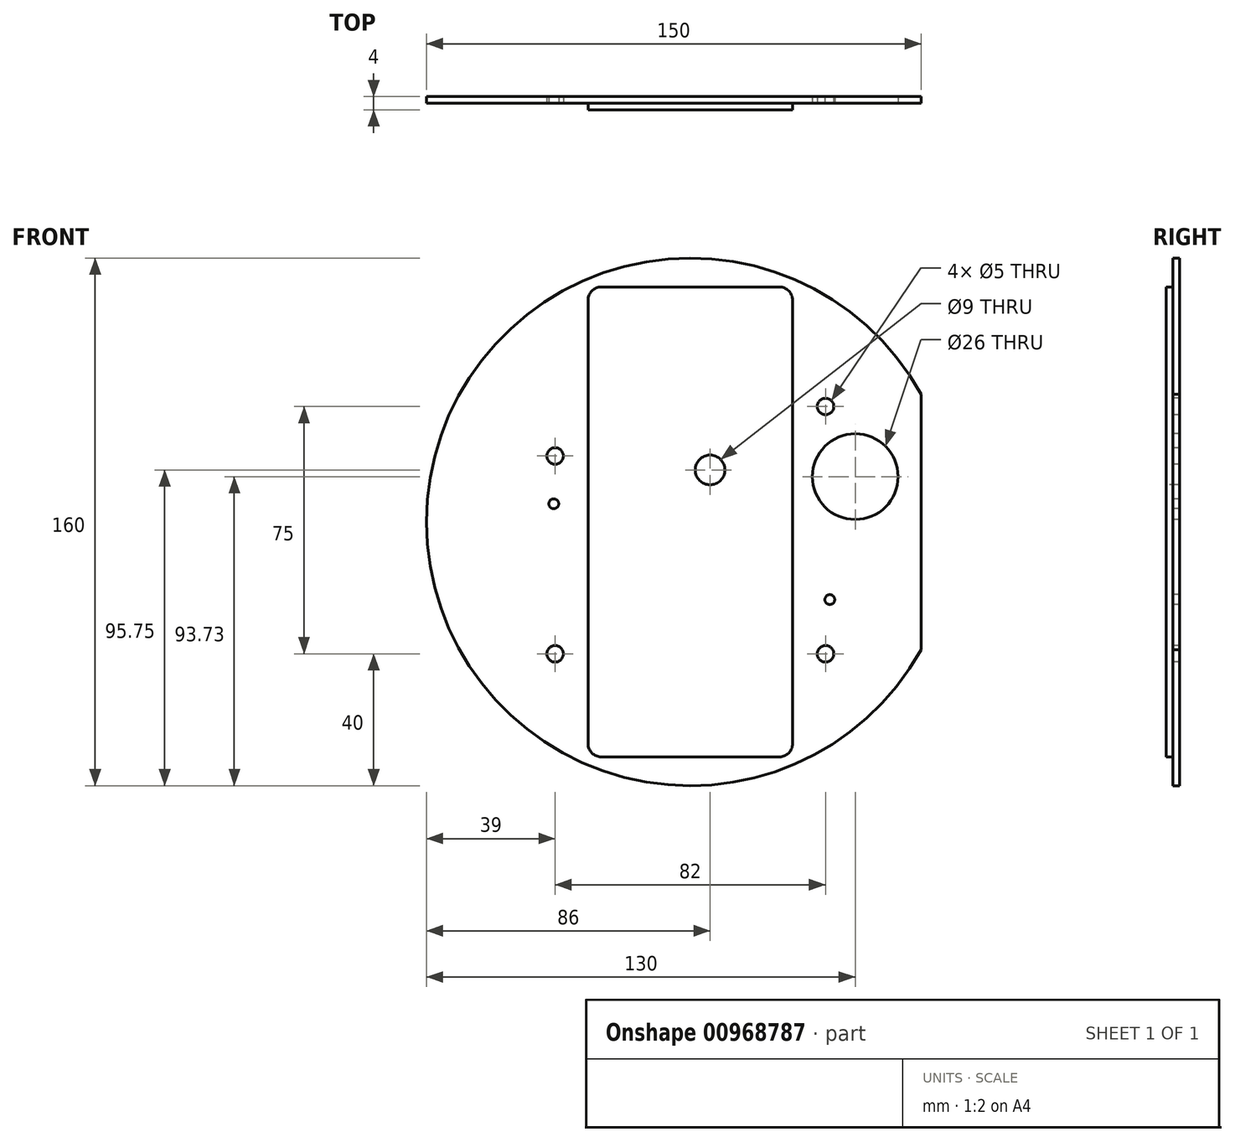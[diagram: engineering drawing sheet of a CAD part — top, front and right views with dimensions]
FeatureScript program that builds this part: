
annotation { "Feature Type Name" : "Feature", "Feature Type Description" : "" }
export const myFeature = defineFeature(function(context is Context, id is Id, definition is map)
    precondition{}
    {
        {
            var Q0;
            Q0=qCreatedBy(makeId("Front.planeOp"),FACE);
            var sketch = newSketch(context, id + "F0", { "sketchPlane" : qUnion([Q0])});
            skArc(sketch, "E0", {"start": v(70, -38.73) * mm, "mid": v(-80, 0) * mm, "end": v(70, 38.73) * mm});
            skLineSegment(sketch, "E1", {"start": v(70, 38.73) * mm, "end": v(70, -38.73) * mm});
            skSolve(sketch);
        }
        {
            var Q0;
            Q0 = qSketchRegion(id + "F0", true);
            extrude(context, id + "F1", {"entities" : qUnion([Q0]), "depth" : 2 * mm, "offsetDistance" : 25 * mm});
        }
        {
            var Q0;
            Q0=makeQuery(id+"F1.opExtrude","CAP_FACE",FACE,{"disambiguationData":[OSD([sQuery(id+"F0.wireOp",EDGE,"E0"),sQuery(id+"F0.wireOp",EDGE,"E1")])],"isStart":false});
            var sketch = newSketch(context, id + "F2", { "sketchPlane" : qUnion([Q0])});
            skLineSegment(sketch, "E2.bottom", {"start": v(-31, 71.25) * mm, "end": v(31, 71.25) * mm});
            skLineSegment(sketch, "E2.top", {"start": v(-31, -71.25) * mm, "end": v(31, -71.25) * mm});
            skLineSegment(sketch, "E2.left", {"start": v(-31, 71.25) * mm, "end": v(-31, -71.25) * mm});
            skLineSegment(sketch, "E2.right", {"start": v(31, 71.25) * mm, "end": v(31, -71.25) * mm});
            skSolve(sketch);
        }
        {
            var Q0;
            Q0 = qSketchRegion(id + "F2", true);
            extrude(context, id + "F3", {"entities" : qUnion([Q0]), "operationType" : NewBodyOperationType.ADD, "depth" : 2 * mm, "offsetDistance" : 25 * mm});
        }
        {
            var Q0;
            Q0=makeQuery(id+"F3.opExtrude","SWEPT_EDGE",EDGE,{"disambiguationData":[OSD([sQuery(id+"F2.wireOp",EDGE,"E2.top"),sQuery(id+"F2.wireOp",EDGE,"E2.left")])]});
            var Q1;
            Q1=makeQuery(id+"F3.opExtrude","SWEPT_EDGE",EDGE,{"disambiguationData":[OSD([sQuery(id+"F2.wireOp",EDGE,"E2.top"),sQuery(id+"F2.wireOp",EDGE,"E2.right")])]});
            var Q2;
            Q2=makeQuery(id+"F3.opExtrude","SWEPT_EDGE",EDGE,{"disambiguationData":[OSD([sQuery(id+"F2.wireOp",EDGE,"E2.bottom"),sQuery(id+"F2.wireOp",EDGE,"E2.right")])]});
            var Q3;
            Q3=makeQuery(id+"F3.opExtrude","SWEPT_EDGE",EDGE,{"disambiguationData":[OSD([sQuery(id+"F2.wireOp",EDGE,"E2.bottom"),sQuery(id+"F2.wireOp",EDGE,"E2.left")])]});
            fillet(context, id + "F4", {"entities" : qUnion([Q0, Q1, Q2, Q3]), "radius" : 4 * mm, "tangentPropagation" : true, "allowEdgeOverflow" : false});
        }
        {
            var Q0;
            Q0=makeQuery(id+"F3.opExtrude","CAP_FACE",FACE,{"disambiguationData":[OSD([sQuery(id+"F2.wireOp",EDGE,"E2.bottom"),sQuery(id+"F2.wireOp",EDGE,"E2.top"),sQuery(id+"F2.wireOp",EDGE,"E2.left"),sQuery(id+"F2.wireOp",EDGE,"E2.right")])],"isStart":false});
            var sketch = newSketch(context, id + "F5", { "sketchPlane" : qUnion([Q0])});
            skCircle(sketch, "E3", {"center": v(6, 15.75) * mm, "radius": 4.5 * mm});
            skSolve(sketch);
        }
        {
            var Q0;
            Q0 = qSketchRegion(id + "F5", true);
            extrude(context, id + "F6", {"entities" : qUnion([Q0]), "operationType" : NewBodyOperationType.REMOVE, "oppositeDirection" : true, "depth" : 4 * mm, "offsetDistance" : 25 * mm});
        }
        {
            var Q0;
            Q0=makeQuery(id+"F1.opExtrude","CAP_FACE",FACE,{"disambiguationData":[OSD([sQuery(id+"F0.wireOp",EDGE,"E0"),sQuery(id+"F0.wireOp",EDGE,"E1")])],"isStart":false});
            var sketch = newSketch(context, id + "F7", { "sketchPlane" : qUnion([Q0])});
            skCircle(sketch, "E4", {"center": v(50, 13.73) * mm, "radius": 13 * mm});
            skSolve(sketch);
        }
        {
            var Q0;
            Q0 = qSketchRegion(id + "F7", true);
            extrude(context, id + "F8", {"entities" : qUnion([Q0]), "operationType" : NewBodyOperationType.REMOVE, "oppositeDirection" : true, "depth" : 2 * mm, "offsetDistance" : 25 * mm});
        }
        {
            var Q0;
            Q0=makeQuery(id+"F1.opExtrude","CAP_FACE",FACE,{"disambiguationData":[OSD([sQuery(id+"F0.wireOp",EDGE,"E0"),sQuery(id+"F0.wireOp",EDGE,"E1")])],"isStart":false});
            var sketch = newSketch(context, id + "F9", { "sketchPlane" : qUnion([Q0])});
            skCircle(sketch, "E5", {"center": v(-41, 20) * mm, "radius": 2.5 * mm});
            skCircle(sketch, "E6", {"center": v(-41, -40) * mm, "radius": 2.5 * mm});
            skCircle(sketch, "E7", {"center": v(41, 35) * mm, "radius": 2.5 * mm});
            skCircle(sketch, "E8", {"center": v(41, -40) * mm, "radius": 2.5 * mm});
            skSolve(sketch);
        }
        {
            var Q0;
            Q0 = qSketchRegion(id + "F9", true);
            extrude(context, id + "F10", {"entities" : qUnion([Q0]), "operationType" : NewBodyOperationType.REMOVE, "oppositeDirection" : true, "depth" : 2 * mm, "offsetDistance" : 25 * mm});
        }
        {
            var Q0;
            Q0=makeQuery(id+"F1.opExtrude","CAP_FACE",FACE,{"disambiguationData":[OSD([sQuery(id+"F0.wireOp",EDGE,"E0"),sQuery(id+"F0.wireOp",EDGE,"E1")])],"isStart":false});
            var sketch = newSketch(context, id + "F11", { "sketchPlane" : qUnion([Q0])});
            skCircle(sketch, "E9", {"center": v(-41.4, 5.5) * mm, "radius": 1.5 * mm});
            skCircle(sketch, "E10", {"center": v(42.3, -23.55) * mm, "radius": 1.5 * mm});
            skSolve(sketch);
        }
        {
            var Q0;
            Q0 = qSketchRegion(id + "F11", true);
            extrude(context, id + "F12", {"entities" : qUnion([Q0]), "operationType" : NewBodyOperationType.REMOVE, "oppositeDirection" : true, "depth" : 2 * mm, "offsetDistance" : 25 * mm});
        }
    });
